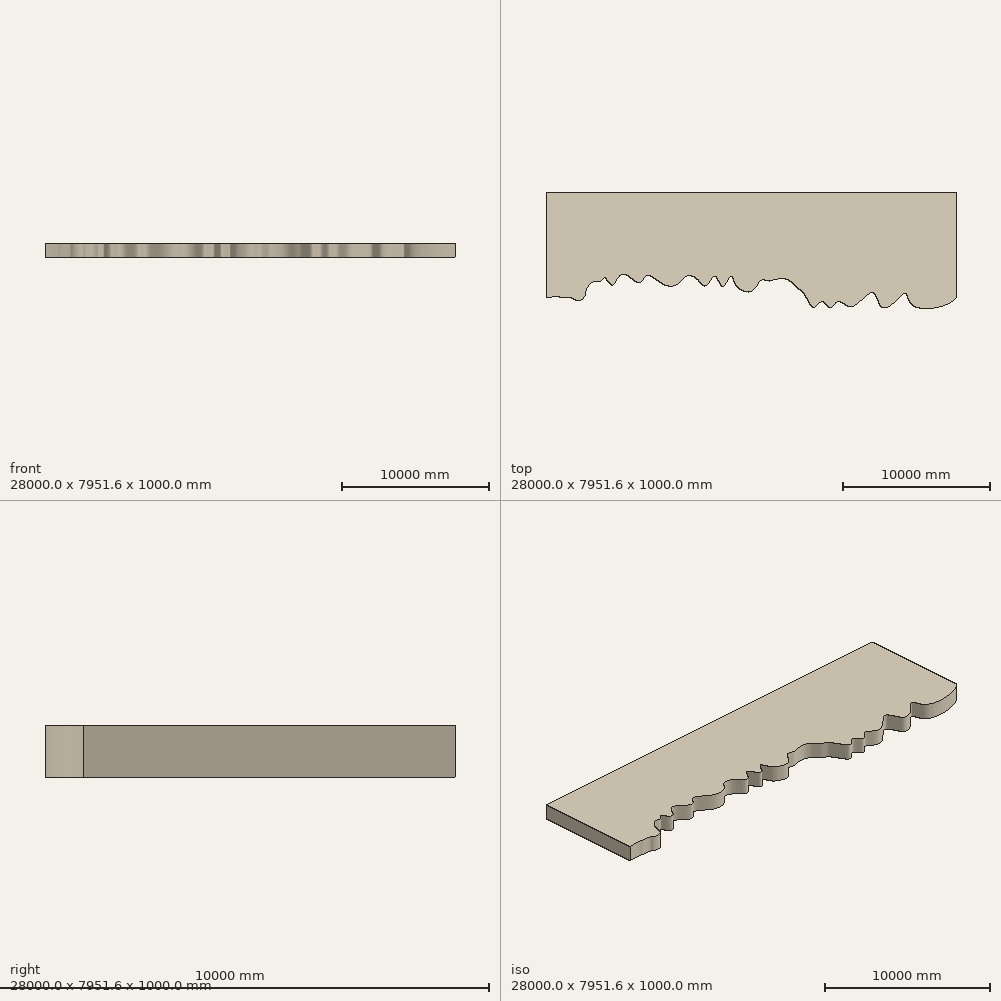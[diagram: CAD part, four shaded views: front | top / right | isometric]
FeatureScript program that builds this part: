
annotation { "Feature Type Name" : "Feature", "Feature Type Description" : "" }
export const myFeature = defineFeature(function(context is Context, id is Id, definition is map)
    precondition{}
    {
        {
            var Q0;
            Q0=qCreatedBy(makeId("Top.planeOp"),FACE);
            var sketch = newSketch(context, id + "F0", { "sketchPlane" : qUnion([Q0])});
            skFitSpline(sketch, "E0", {"points": [v(14882.1, -3829.02) * mm, v(11868.95, -4318.87) * mm, v(11411.06, -3497.16) * mm, v(10664.46, -4134.62) * mm, v(9741.7, -4407.35) * mm, v(9150.78, -3467.67) * mm, v(7719.15, -4424.51) * mm, v(6801.81, -4062.77) * mm, v(6282.6, -4503.8) * mm, v(5713.87, -4085.89) * mm, v(5140.63, -4478.9) * mm, v(4456.5, -3504.15) * mm, v(4006.03, -3130.53) * mm, v(3292.24, -2557.86) * mm, v(2360.64, -2610.51) * mm, v(2121.9, -2666) * mm, v(1606.78, -2603.55) * mm, v(1311.12, -2936.26) * mm, v(871.3, -3387.8) * mm, v(320.46, -3335.43) * mm, v(-198.16, -2937.3) * mm, v(-516.46, -2374.85) * mm, v(-1086.15, -3047.2) * mm, v(-1604.32, -2352.32) * mm, v(-2197.2, -2995.52) * mm, v(-2864.06, -2510.92) * mm, v(-3585.32, -2357.68) * mm, v(-4150.48, -2891.27) * mm, v(-5142.29, -2888.49) * mm, v(-6227.5, -2306.47) * mm, v(-6748.3, -2796.66) * mm, v(-7632.44, -2261.4) * mm, v(-8088.97, -2309.7) * mm, v(-8441.5, -2815.22) * mm, v(-8636.61, -2947.1) * mm, v(-8949.1, -2663.04) * mm, v(-9139.5, -2444.77) * mm, v(-9432.21, -2694.95) * mm, v(-9632.13, -2691.85) * mm, v(-9927.2, -2727.7) * mm, v(-10378.4, -3246.28) * mm, v(-10455.4, -3599.76) * mm, v(-10745.93, -3980.7) * mm, v(-11238.54, -3924.32) * mm, v(-11395.6, -3828.82) * mm, v(-12007.05, -3796.97) * mm, v(-12165.93, -3766.66) * mm, v(-13117.9, -3803.46) * mm], "startDerivative": vector(-38606.6, -46370.21) * mm, "endDerivative": vector(-52653.07, -8275.73) * mm});
            skLineSegment(sketch, "E1", {"start": v(-13117.9, -3803.46) * mm, "end": v(-13117.9, -4607.43) * mm});
            skLineSegment(sketch, "E2", {"start": v(-13117.9, -4607.43) * mm, "end": v(14882.1, -4607.43) * mm});
            skLineSegment(sketch, "E3", {"start": v(14882.1, -4607.43) * mm, "end": v(14882.1, -3829.02) * mm});
            skLineSegment(sketch, "E4", {"start": v(-13117.9, -3803.46) * mm, "end": v(-13117.9, 3392.57) * mm});
            skLineSegment(sketch, "E5", {"start": v(-13117.9, 3392.57) * mm, "end": v(14882.1, 3392.57) * mm});
            skLineSegment(sketch, "E6", {"start": v(14882.1, 3392.57) * mm, "end": v(14882.1, -3829.02) * mm});
            skSolve(sketch);
        }
        {
            var Q0;
            Q0=makeQuery(id+"F0.imprint","IMPRINT",FACE,{"disambiguationData":[TD([[makeQuery(id+"F0.imprint","IMPRINT",EDGE,{"derivedFrom":sQuery(id+"F0.wireOp",EDGE,"E0")}),-1.0]])]});
            extrude(context, id + "F1", {"entities" : qUnion([Q0]), "depth" : 1000 * mm, "offsetDistance" : 25 * mm});
        }
    });
